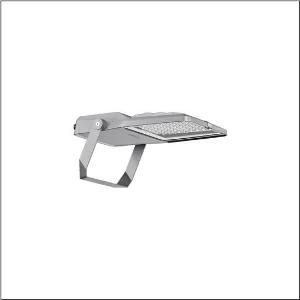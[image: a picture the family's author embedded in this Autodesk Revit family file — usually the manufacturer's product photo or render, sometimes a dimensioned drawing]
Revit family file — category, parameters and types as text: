
# Revit family: floodlight_fl_21_mini___pl33t_5xa7775b2f1a_fedb
name_source: partatom
category: Lighting Fixtures
units: mm (PartAtom-declared; Revit-internal decimal feet)

## family parameters
Cut with Voids When Loaded = No
Host = Face
Light Source = No
Part Type = Normal
Room Calculation Point = No
Round Connector Dimension = Use Diameter
Shared = No

## types (1)
- --- (1 x LED, 6150 lm, 45.7 W, 3000K)
    Apparent Load = 46 VA
    CIE Flux Codes = 26 75 99 100 100
    Color Rendering = 70
    Color Temperature = 3000K
    Default Elevation = 1800 mm
    Description = Floodlight FL 21 mini, floodlight, primary light control with lens, of PMMA, primary optical cover: protective disc, of toughened safety glass, transparent, light distribution: PL33T, light emission: direct distribution, installation type: surface-mounted, LED, High Power LED, rated luminous flux: 6.150lm, luminous efficacy: 135lm/W, light colour: 730, colour temperature: 3000K, control: flexible luminous flux parameterisation, time-dependent luminous flux control, constant luminous flux control, overheat protection, presetting dimming logarithmic, with terminal, 6-pole, mains connection: 220..240V, AC, 50/60Hz, start of lifetime: 46W, end of service life: 48W, reduction: 22W, luminaire housing, of diecast aluminium, powder-coated, Siteco® metallic grey (DB 702S), corrosivity category C5 mid according to DIN EN ISO 12944, sealing non-destructively replaceable, mounting bracket, of steel, galvanised, powder-coated, Siteco® metallic grey (DB 702S), Smart Interface above, protection rating (complete): IP66, insulation class (complete): insulation class II (safety insulation), certification: CE, ENEC, VDE, protection symbol: D, impact resistance: IK08, permissible operating ambient temperature: -40..+40°C, permissible operating ambient temperature for outdoor applications: -40..+50°C, standard: DIN EN 12944, LABS conformity tested according to VDMA 24364:2018-05, packaging unit: 1 piece

Light Distribution: PL33T
    Height = 70 mm
    Lamp = 1 x LED
    Lamp Light Flux = 6150 lm
    Lamp Power = 45.7 W
    Lamp count = 1
    Length = 485 mm
    Luminous efficacy = 135 lm/W
    Manufacturer = Siteco
    ModVariant = No
    Model = 5XA7775B2F1A
    Number of Poles = 1
    OnlyDefault = Yes
    Power Factor = 1
    Product Name = Floodlight FL 21 mini | PL33T
    Product group = floodlight | pylon annexe
    ProductGroupID = 6200
    Protection Class = Protection class II
    Protection Degree = IP 66
    RLX_Detail_Level = 1
    RLX_Emergency_Light_Flux = 0 lm
    RLX_Emergency_Type = 0
    RLX_Emergency_Type_DB = No
    RlxData = <blob elided: 95825 chars, md5=51f4a733>
    Socket = socket
    Standby Power = 0 W
    System Light Flux = 6150 lm
    System Power = 46 W
    Type Comments = factory setting: luminous flux: 100 % | dim-lin: 254 | 463 mA
    Type Image = l_1006845.jpg
    URL = http://relux.com
    VarID = @adj_081191
    Voltage = 0 V
    Weight = 0.00 kg
    Width = 337 mm

## geometry (parser evidence)
native form markers: Blend x4, Sweep x12
no freeform markers — native parametric forms only
